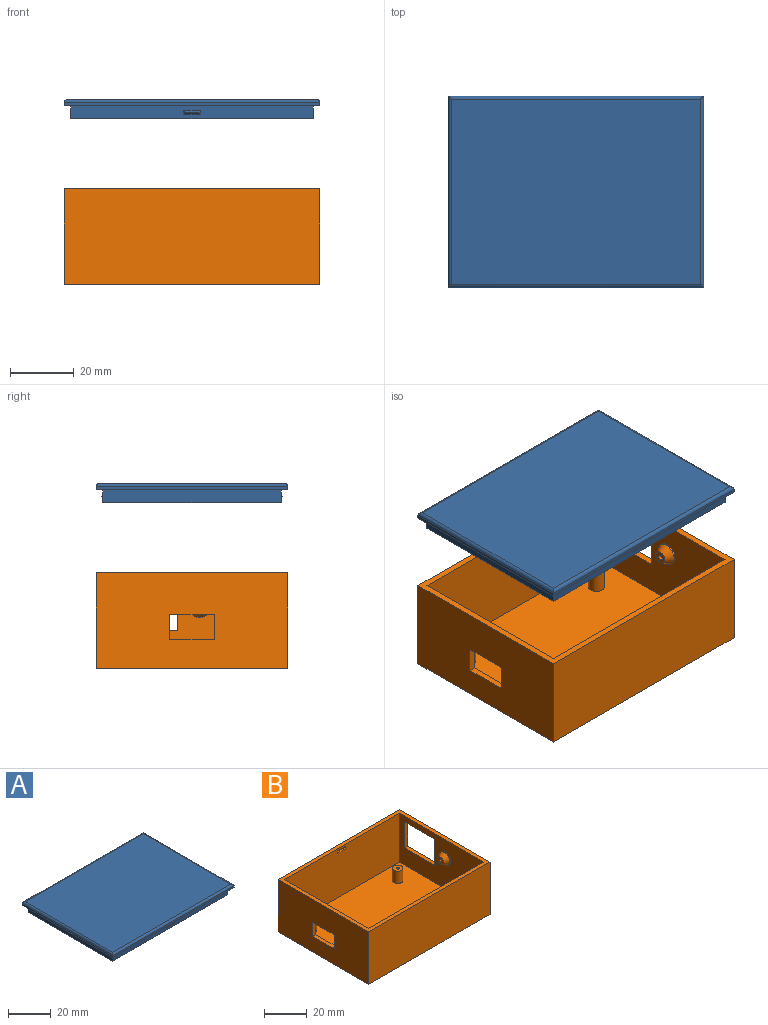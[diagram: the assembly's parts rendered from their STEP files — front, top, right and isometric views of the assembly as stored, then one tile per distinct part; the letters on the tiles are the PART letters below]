
ASSEMBLY  parts=2 mates=1
PART A: 25 faces, bbox 80x60x6 mm
  f0: plane 76x4mm, normal (0,1,0), area 298.1mm2, adj f6,f8,f9,f10,f21,f22,f23,f24
  f1: plane 80x1mm, normal (0,1,0), area 80mm2, adj f2,f4,f6,f11
  f2: plane 60x1mm, normal (-1,0,0), area 60mm2, adj f1,f3,f6,f12
  f3: plane 80x1mm, normal (0,-1,0), area 80mm2, adj f2,f4,f6,f14
  f4: plane 60x1mm, normal (1,0,0), area 60mm2, adj f1,f3,f6,f13
  f5: plane 78x58mm, normal (0,0,1), area 4524mm2, adj f11,f12,f13,f14
  f6: plane 80x60mm, normal (0,0,-1), area 544mm2, adj f0,f1,f2,f3,f4,f7,f8,f9
  f7: plane 76x4mm, normal (0,-1,0), area 298.1mm2, adj f6,f8,f9,f10,f16,f17,f18,f19
  f8: plane 56x4mm, normal (-1,0,0), area 224mm2, adj f0,f6,f7,f10
  f9: plane 56x4mm, normal (1,0,0), area 224mm2, adj f0,f6,f7,f10
  f10: plane 76x56mm, normal (0,0,-1), area 4256mm2, adj f0,f7,f8,f9
  f11: cylinder r=1mm len=80mm, axis (1,0,0), area 124.5mm2, adj f1,f5,f12,f13
  f12: cylinder r=1mm len=60mm, axis (0,1,0), area 93.1mm2, adj f2,f5,f11,f14
  f13: cylinder r=1mm len=60mm, axis (0,-1,0), area 93.1mm2, adj f4,f5,f11,f14
  f14: cylinder r=1mm len=80mm, axis (-1,0,0), area 124.5mm2, adj f3,f5,f12,f13
  f15: plane 4.11x0.16mm, normal (0,-1,0), area 0.6mm2, adj f16,f17,f18,f19
  f16: plane 1.16x0.5mm, normal (0.71,-0.71,0), area 0.5mm2, adj f7,f15,f17,f18
  f17: plane 5.11x0.5mm, normal (0,-0.71,-0.71), area 3.3mm2, adj f7,f15,f16,f19
  f18: plane 5.11x0.5mm, normal (0,-0.71,0.71), area 3.3mm2, adj f7,f15,f16,f19
  f19: plane 1.16x0.5mm, normal (-0.71,-0.71,0), area 0.5mm2, adj f7,f15,f17,f18
  f20: plane 4.11x0.16mm, normal (0,1,0), area 0.6mm2, adj f21,f22,f23,f24
  f21: plane 1.16x0.5mm, normal (0.71,0.71,0), area 0.5mm2, adj f0,f20,f22,f23
  f22: plane 5.11x0.5mm, normal (0,0.71,-0.71), area 3.3mm2, adj f0,f20,f21,f24
  f23: plane 5.11x0.5mm, normal (0,0.71,0.71), area 3.3mm2, adj f0,f20,f21,f24
  f24: plane 1.16x0.5mm, normal (-0.71,0.71,0), area 0.5mm2, adj f0,f20,f22,f23
PART B: 50 faces, bbox 80x60x30 mm
  f0: plane 76x28mm, normal (0,1,0), area 2121.1mm2, adj f2,f4,f5,f10,f40,f41,f42,f43
  f1: plane 60x30mm, normal (1,0,0), area 1500mm2, adj f5,f6,f7,f8,f31,f32,f33,f34
  f2: plane 56x28mm, normal (-1,0,0), area 1229.5mm2, adj f0,f5,f9,f10,f31,f32,f33,f34
  f3: plane 60x30mm, normal (-1,0,0), area 1688mm2, adj f5,f6,f7,f8,f27,f28,f29,f30
  f4: plane 56x28mm, normal (1,0,0), area 1456mm2, adj f0,f5,f9,f10,f27,f28,f29,f30
  f5: plane 80x60mm, normal (0,0,1), area 544mm2, adj f0,f1,f2,f3,f4,f6,f7,f9
  f6: plane 80x30mm, normal (0,1,0), area 2400mm2, adj f1,f3,f5,f8
  f7: plane 80x30mm, normal (0,-1,0), area 2400mm2, adj f1,f3,f5,f8
  f8: plane 80x60mm, normal (0,0,-1), area 4800mm2, adj f1,f3,f6,f7
  f9: plane 76x28mm, normal (0,-1,0), area 2121.1mm2, adj f2,f4,f5,f10,f45,f46,f47,f48
  f10: plane 76x56mm, normal (0,0,1), area 4177.5mm2, adj f0,f2,f4,f9,f12,f16,f20,f24
  f11: cylinder r=0.75mm len=7mm, axis (0,0,-1), area 33mm2, adj f13,f14
  f12: cylinder r=2.5mm len=7mm, axis (0,0,-1), area 110mm2, adj f10,f13
  f13: plane 5x5mm, normal (0,0,1), area 17.9mm2, adj f11,f12
  f14: plane 1.5x1.5mm, normal (0,0,1), area 1.8mm2, adj f11
  f15: cylinder r=0.75mm len=7mm, axis (0,0,-1), area 33mm2, adj f17,f18
  f16: cylinder r=2.5mm len=7mm, axis (0,0,-1), area 110mm2, adj f10,f17
  f17: plane 5x5mm, normal (0,0,1), area 17.9mm2, adj f15,f16
  f18: plane 1.5x1.5mm, normal (0,0,1), area 1.8mm2, adj f15
  f19: cylinder r=0.75mm len=7mm, axis (0,0,-1), area 33mm2, adj f21,f22
  f20: cylinder r=2.5mm len=7mm, axis (0,0,-1), area 110mm2, adj f10,f21
  f21: plane 5x5mm, normal (0,0,1), area 17.9mm2, adj f19,f20
  f22: plane 1.5x1.5mm, normal (0,0,1), area 1.8mm2, adj f19
  f23: cylinder r=0.75mm len=7mm, axis (0,0,-1), area 33mm2, adj f25,f26
  f24: cylinder r=2.5mm len=7mm, axis (0,0,-1), area 110mm2, adj f10,f25
  f25: plane 5x5mm, normal (0,0,1), area 17.9mm2, adj f23,f24
  f26: plane 1.5x1.5mm, normal (0,0,1), area 1.8mm2, adj f23
  f27: plane 14x2mm, normal (0,0,-1), area 28mm2, adj f3,f4,f28,f30
  f28: plane 8x2mm, normal (0,-1,0), area 16mm2, adj f3,f4,f27,f29
  f29: plane 14x2mm, normal (0,0,1), area 28mm2, adj f3,f4,f28,f30
  f30: plane 8x2mm, normal (0,1,0), area 16mm2, adj f3,f4,f27,f29
  f31: plane 15x2mm, normal (0,-1,0), area 30mm2, adj f1,f2,f32,f34
  f32: plane 20x2mm, normal (0,0,-1), area 40mm2, adj f1,f2,f31,f33
  f33: plane 15x2mm, normal (0,1,0), area 30mm2, adj f1,f2,f32,f34
  f34: plane 20x2mm, normal (0,0,1), area 40mm2, adj f1,f2,f31,f33
  f35: cylinder r=0.75mm len=3mm, axis (1,0,0), area 14.1mm2, adj f37,f38
  f36: cylinder r=3.5mm len=7mm, axis (1,0,0), area 8.8mm2, adj f2,f49
  f37: plane 4x4mm, normal (-1,0,0), area 10.8mm2, adj f35,f49
  f38: plane 1.5x1.5mm, normal (-1,0,0), area 1.8mm2, adj f35
  f39: plane 4.27x0.31mm, normal (0,1,0), area 1.3mm2, adj f40,f41,f42,f43
  f40: plane 1.31x0.5mm, normal (0.71,0.71,0), area 0.6mm2, adj f0,f39,f41,f42
  f41: plane 5.27x0.5mm, normal (0,0.71,0.71), area 3.4mm2, adj f0,f39,f40,f43
  f42: plane 5.27x0.5mm, normal (0,0.71,-0.71), area 3.4mm2, adj f0,f39,f40,f43
  f43: plane 1.31x0.5mm, normal (-0.71,0.71,0), area 0.6mm2, adj f0,f39,f41,f42
  f44: plane 4.27x0.31mm, normal (0,-1,0), area 1.3mm2, adj f45,f46,f47,f48
  f45: plane 1.31x0.5mm, normal (0.71,-0.71,0), area 0.6mm2, adj f9,f44,f46,f47
  f46: plane 5.27x0.5mm, normal (0,-0.71,0.71), area 3.4mm2, adj f9,f44,f45,f48
  f47: plane 5.27x0.5mm, normal (0,-0.71,-0.71), area 3.4mm2, adj f9,f44,f45,f48
  f48: plane 1.31x0.5mm, normal (-0.71,-0.71,0), area 0.6mm2, adj f9,f44,f46,f47
  f49: cone r=2mm half-angle=30deg, axis (1,0,0), area 51.8mm2, adj f36,f37
PLACE A t=(-0.09,0,26.15)mm
PLACE B t=(-0.09,0,0.21)mm fixed
MATE slider B.f5 <-> A.f6  axis (0,0,1) through (39.91,30,30.21)mm
